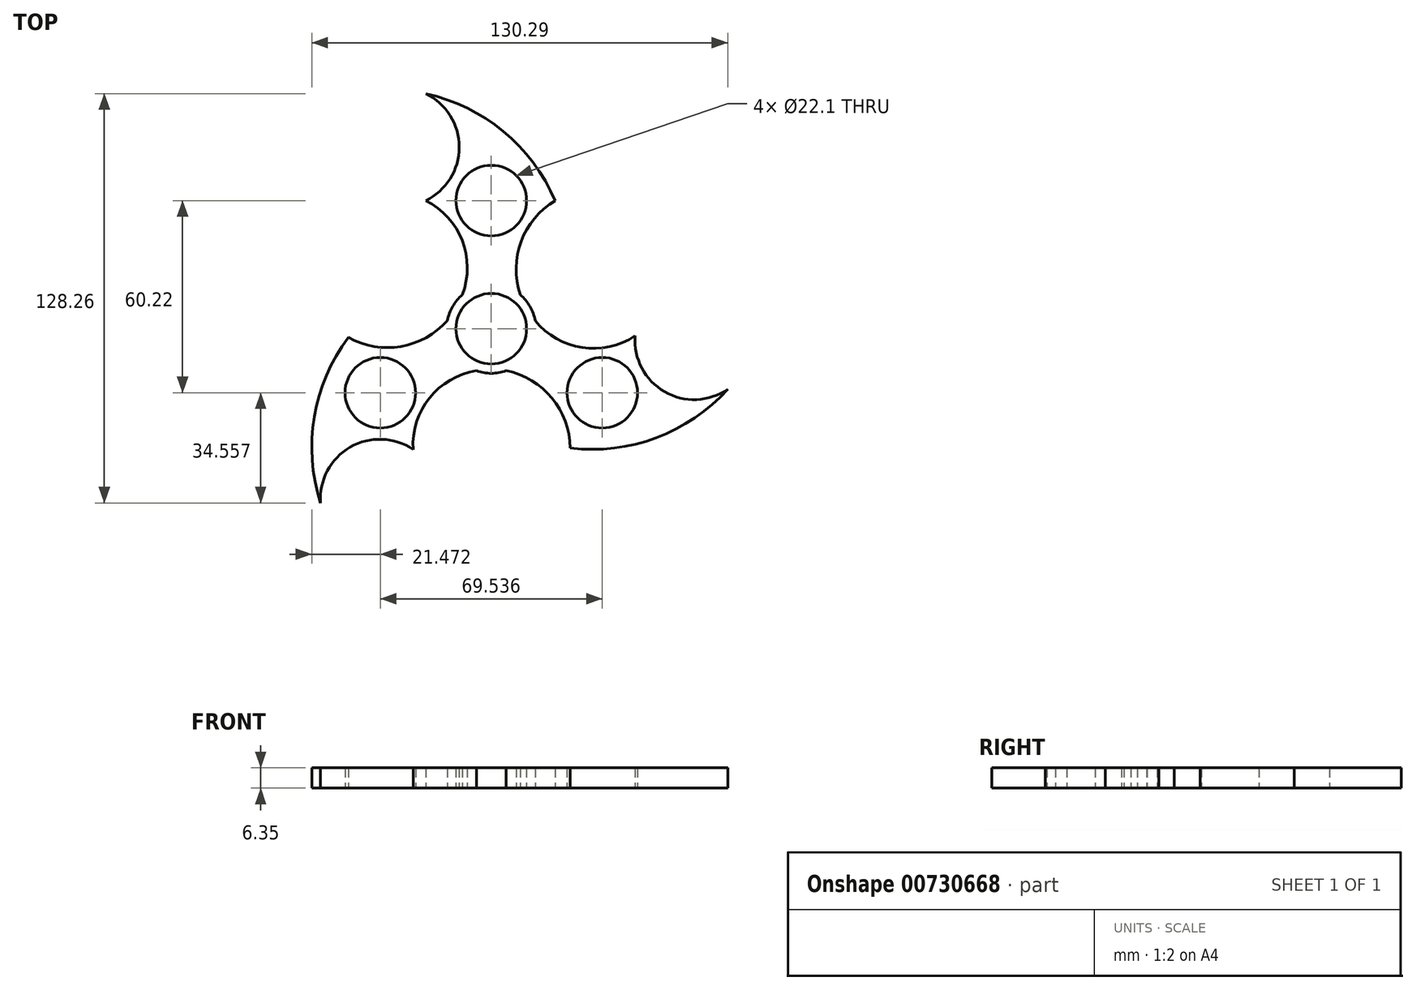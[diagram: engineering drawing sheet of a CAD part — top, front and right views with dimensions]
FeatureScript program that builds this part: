
annotation { "Feature Type Name" : "Feature", "Feature Type Description" : "" }
export const myFeature = defineFeature(function(context is Context, id is Id, definition is map)
    precondition{}
    {
        {
            var Q0;
            Q0=qCreatedBy(makeId("Top.planeOp"),FACE);
            var sketch = newSketch(context, id + "F0", { "sketchPlane" : qUnion([Q0])});
            skCircle(sketch, "E0", {"center": v(0, 0) * mm, "radius": 11.05 * mm});
            skArc(sketch, "E1", {"start": v(-9.06, 10.63) * mm, "mid": v(-12.1, 6.98) * mm, "end": v(-13.74, 2.53) * mm});
            skLineSegment(sketch, "E2", {"start": v(0, 0) * mm, "end": v(0, 11.05) * mm});
            skCircle(sketch, "E3", {"center": v(0, 40.15) * mm, "radius": 11.05 * mm});
            skArc(sketch, "E4", {"start": v(-9.06, 10.63) * mm, "mid": v(-9.13, 27.6) * mm, "end": v(-20.57, 40.15) * mm});
            skArc(sketch, "E5", {"start": v(20, 40.15) * mm, "mid": v(9.34, 27.32) * mm, "end": v(9.06, 10.63) * mm});
            skArc(sketch, "E6", {"start": v(-20.57, 40.15) * mm, "mid": v(-10.04, 56.89) * mm, "end": v(-20.57, 73.63) * mm});
            skArc(sketch, "E7", {"start": v(20, 40.15) * mm, "mid": v(3.8, 61.83) * mm, "end": v(-20.57, 73.63) * mm});
            skCircle(sketch, "E8.1.0", {"center": v(-34.77, -20.07) * mm, "radius": 11.05 * mm});
            skArc(sketch, "E8.1.1", {"start": v(-4.68, -13.16) * mm, "mid": v(-19.34, -21.71) * mm, "end": v(-24.48, -37.89) * mm});
            skArc(sketch, "E8.1.2", {"start": v(-24.48, -37.89) * mm, "mid": v(-44.24, -37.14) * mm, "end": v(-53.48, -54.63) * mm});
            skArc(sketch, "E8.1.3", {"start": v(-44.77, -2.75) * mm, "mid": v(-55.45, -27.63) * mm, "end": v(-53.48, -54.63) * mm});
            skArc(sketch, "E8.1.4", {"start": v(-44.77, -2.75) * mm, "mid": v(-28.32, -5.57) * mm, "end": v(-13.74, 2.53) * mm});
            skCircle(sketch, "E8.2.0", {"center": v(34.77, -20.07) * mm, "radius": 11.05 * mm});
            skArc(sketch, "E8.2.1", {"start": v(13.74, 2.53) * mm, "mid": v(28.47, -5.9) * mm, "end": v(45.05, -2.26) * mm});
            skArc(sketch, "E8.2.2", {"start": v(45.05, -2.26) * mm, "mid": v(54.29, -19.75) * mm, "end": v(74.05, -19) * mm});
            skArc(sketch, "E8.2.3", {"start": v(24.77, -37.4) * mm, "mid": v(51.65, -34.2) * mm, "end": v(74.05, -19) * mm});
            skArc(sketch, "E8.2.4", {"start": v(24.77, -37.4) * mm, "mid": v(18.99, -21.74) * mm, "end": v(4.68, -13.16) * mm});
            skArc(sketch, "E9.trimOffspring", {"start": v(-4.68, -13.16) * mm, "mid": v(0, -13.97) * mm, "end": v(4.68, -13.16) * mm});
            skArc(sketch, "E10.trimOffspring", {"start": v(13.74, 2.53) * mm, "mid": v(12.1, 6.98) * mm, "end": v(9.06, 10.63) * mm});
            skSolve(sketch);
        }
        {
            var Q0;
            Q0 = qSketchRegion(id + "F0", true);
            extrude(context, id + "F1", {"entities" : qUnion([Q0]), "depth" : 6.35 * mm, "offsetDistance" : 25.4 * mm});
        }
    });
